# Revit family: 0005350
name_source: partatom
category: Lighting Fixtures
revit_build: Autodesk Revit 2017 (Build: 20190507_1515(x64)
units: mm (PartAtom-declared; Revit-internal decimal feet)

## family parameters
Cut with Voids When Loaded = No
Host = Face
Light Source = Yes
OmniClass Number = 23.80.70.00
OmniClass Title = Lighting
Part Type = Normal
Room Calculation Point = No
Round Connector Dimension = Use Diameter
Shared = No

## types (1)
- 0005350 OBICO IP65 740LM 2CCT DIM WHT
    Apparent Load = 9 VA
    Assembly Code = D5020200
    AssetType = Fixed
    ClassificationName = Uniclass2015
    ClassificationValue = EF_70_80
    Color Filter = 16777215
    Cost = 0 $
    Default Elevation = 1219 mm
    Description = Integrated LED recessed spotlight, 2-axis adjustable (horizontal rotation 360°, vertical tilt 30°) RAL9016 white bezel colour, two temperature light colors selectable: 3000K, 4000K. Lumen output 740lm (4000K), 8.5W, dimmable trailing/leading edge, 38° degree beam angle, aluminium and steel body, low profile 40mm recessed depth, IP65 frontal degree, IK03, loop-in/loop-out terminals for fast wiring, 96mm bezel diameter, 80mm cutout, clear lens. Additional chrome bezel ring included in the packaging. Lifetime: 50.000 hours at L70. Energy Class: A++, A+, A.
    Dimming Lamp Color Temperature Shift = <None>
    DocumentationLiterature = http://www.sylvania-lighting.com
    ElectricShockClassification = Class II
    Emit Shape Visible in Rendering = No
    Emit from Circle Diameter = 610 mm
    IfcExportAs = IfcLightFixtureType
    IfcExportType = IfcLightFixtureType
    ImpactProtectionIndex = IK03
    IngressProtection = IP65/20
    Keynote = 16500
    Lamp = LED
    LampColourRenderingIndex = 80
    LampColourTemperature = 4000 K
    LampMacAdamStep = 6
    LampNominalLuminous = 720 lm
    LampsType = LED
    LuminousEfficacy = 84 lm/W
    Manufacturer = Feilo Sylvania
    ManufacturerName = Feilo Sylvania
    Material = aluminium housing, pc polycarbonate diffuser
    Material_1_SYL = Default
    Material_2_SYL = <By Category>
    Material_3_SYL = <By Category>
    Material_4_SYL = <By Category>
    Model = OBICO IP65 740LM 2CCT DIM ADJ WHT
    ModelNumber = 0005350
    ModelReference = OBICO IP65 740LM 2CCT DIM ADJ WHT
    Name = OBICO IP65 740LM 2CCT DIM ADJ WHT
    NominalDepth = 96 mm
    NominalHeight = 54 mm
    NominalLength = 117 mm
    Photometric Web File = 0005350.ies
    PowerConsumption = 8.5 W
    PowerFactor = 0.9
    Tilt Angle = -90.00°
    Type Image = <None>
    TypeName = OBICO IP65 740LM 2CCT DIM ADJ WHT
    URL = http://www.sylvania-lighting.com
    Voltage = 0 V
    Weight = 1.5 kg

## geometry (parser evidence)
native form markers: Sweep x2
no freeform markers — native parametric forms only
